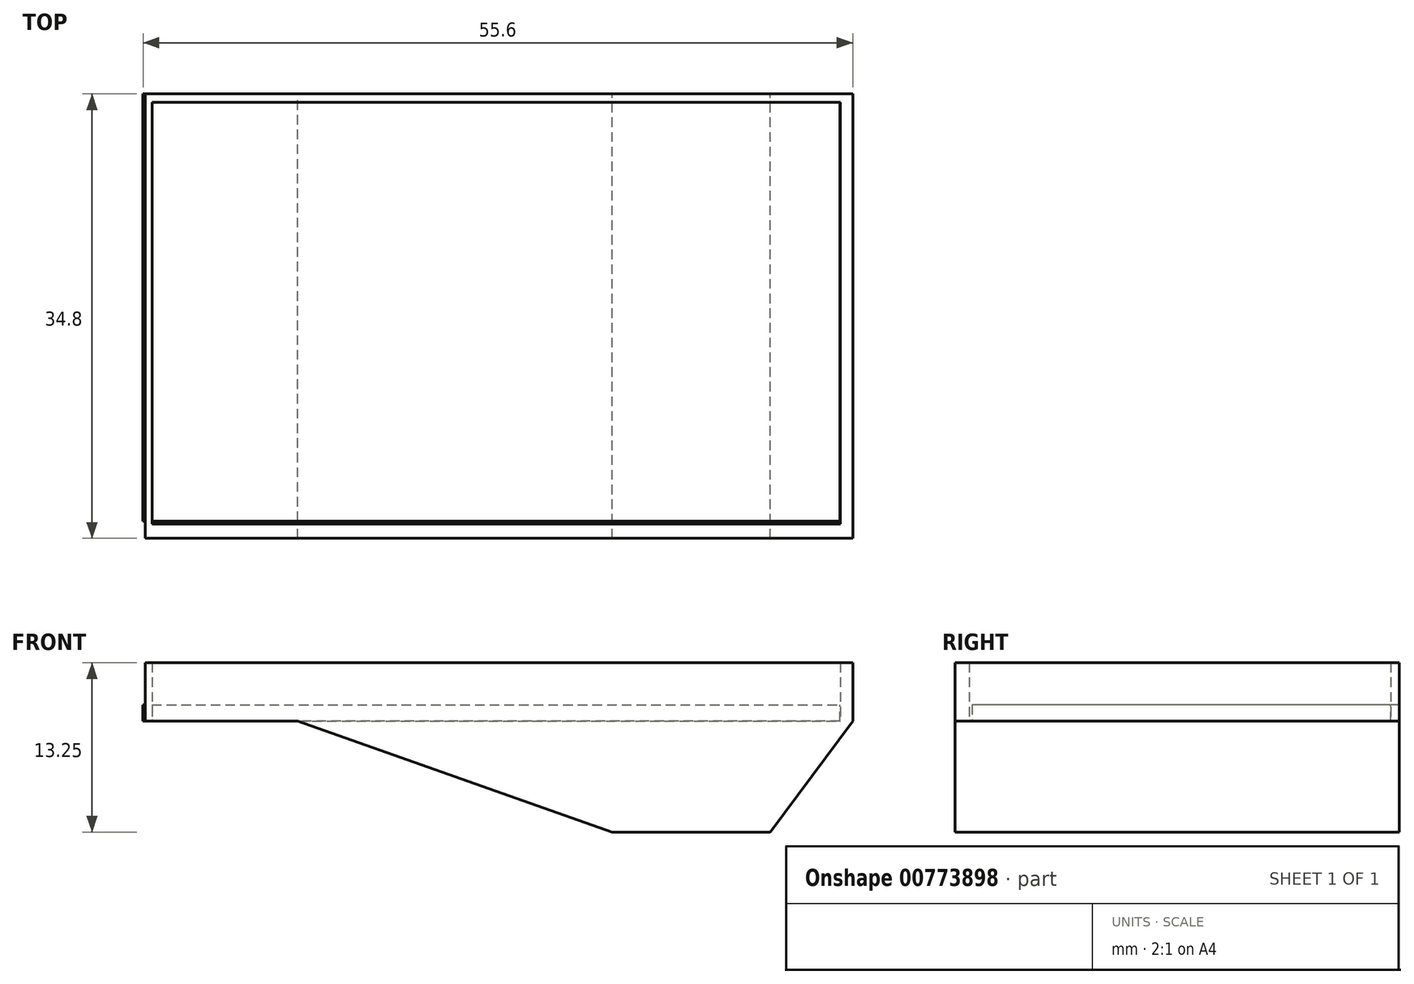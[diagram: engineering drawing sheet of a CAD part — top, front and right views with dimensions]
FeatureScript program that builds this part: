
annotation { "Feature Type Name" : "Feature", "Feature Type Description" : "" }
export const myFeature = defineFeature(function(context is Context, id is Id, definition is map)
    precondition{}
    {
        {
            var Q0;
            Q0=qCreatedBy(makeId("Top.planeOp"),FACE);
            var sketch = newSketch(context, id + "F0", { "sketchPlane" : qUnion([Q0])});
            skLineSegment(sketch, "E0.bottom", {"start": v(5.13, 0) * mm, "end": v(60.56, 0) * mm});
            skLineSegment(sketch, "E0.top", {"start": v(5.13, -34.8) * mm, "end": v(60.56, -34.8) * mm});
            skLineSegment(sketch, "E0.left", {"start": v(5.13, 0) * mm, "end": v(5.13, -34.8) * mm});
            skLineSegment(sketch, "E0.right", {"start": v(60.56, 0) * mm, "end": v(60.56, -34.8) * mm});
            skLineSegment(sketch, "E1.bottom", {"start": v(5.66, -0.66) * mm, "end": v(59.57, -0.66) * mm});
            skLineSegment(sketch, "E1.top", {"start": v(5.66, -33.68) * mm, "end": v(59.57, -33.68) * mm});
            skLineSegment(sketch, "E1.left", {"start": v(5.66, -0.66) * mm, "end": v(5.66, -33.68) * mm});
            skLineSegment(sketch, "E1.right", {"start": v(59.57, -0.66) * mm, "end": v(59.57, -33.68) * mm});
            skSolve(sketch);
        }
        {
            var Q0;
            Q0 = qSketchRegion(id + "F0", true);
            extrude(context, id + "F1", {"entities" : qUnion([Q0]), "depth" : 4.57 * mm, "offsetDistance" : 25.4 * mm});
        }
        {
            var Q0;
            Q0=qCreatedBy(makeId("Top.planeOp"),FACE);
            var sketch = newSketch(context, id + "F2", { "sketchPlane" : qUnion([Q0])});
            skLineSegment(sketch, "E2.bottom", {"start": v(59.56, -33.46) * mm, "end": v(4.96, -33.46) * mm});
            skLineSegment(sketch, "E2.top", {"start": v(59.56, 0) * mm, "end": v(4.96, 0) * mm});
            skLineSegment(sketch, "E2.left", {"start": v(59.56, -33.46) * mm, "end": v(59.56, 0) * mm});
            skLineSegment(sketch, "E2.right", {"start": v(4.96, -33.46) * mm, "end": v(4.96, 0) * mm});
            skSolve(sketch);
        }
        {
            var Q0;
            Q0=makeQuery(id+"F2.imprint","IMPRINT",FACE,{"disambiguationData":[TD([[makeQuery(id+"F2.imprint","IMPRINT",EDGE,{"derivedFrom":sQuery(id+"F2.wireOp",EDGE,"E2.bottom")}),-1.0]])]});
            extrude(context, id + "F3", {"entities" : qUnion([Q0]), "operationType" : NewBodyOperationType.ADD, "depth" : 1.27 * mm, "offsetDistance" : 25.4 * mm});
        }
        {
            var Q0;
            Q0=makeQuery(id+"F3.boolean.opBoolean","MERGE",FACE,{"derivedFrom":[makeQuery(id+"F1.opExtrude","SWEPT_FACE",FACE,{"disambiguationData":[OSD([sQuery(id+"F0.wireOp",EDGE,"E0.bottom")])]}),makeQuery(id+"F3.opExtrude","SWEPT_FACE",FACE,{"disambiguationData":[OSD([sQuery(id+"F2.wireOp",EDGE,"E2.top")])]})]});
            var sketch = newSketch(context, id + "F4", { "sketchPlane" : qUnion([Q0])});
            skLineSegment(sketch, "E3.bottom", {"start": v(-54.09, 0) * mm, "end": v(-41.71, 0) * mm});
            skLineSegment(sketch, "E3.top", {"start": v(-54.09, -8.68) * mm, "end": v(-41.71, -8.68) * mm});
            skLineSegment(sketch, "E4", {"start": v(-60.56, 0) * mm, "end": v(-54.09, -8.68) * mm});
            skLineSegment(sketch, "E5", {"start": v(-41.71, -8.68) * mm, "end": v(-17.07, 0) * mm});
            skLineSegment(sketch, "E6", {"start": v(-17.07, 0) * mm, "end": v(-60.56, 0) * mm});
            skSolve(sketch);
        }
        {
            var Q0;
            Q0 = qSketchRegion(id + "F4", true);
            var Q1;
            Q1=makeQuery(id+"F1.opExtrude","SWEPT_FACE",FACE,{"disambiguationData":[OSD([sQuery(id+"F0.wireOp",EDGE,"E0.top")])]});
            extrude(context, id + "F5", {"entities" : qUnion([Q0]), "operationType" : NewBodyOperationType.ADD, "endBound" : BoundingType.UP_TO_SURFACE, "oppositeDirection" : true, "depth" : 25.4 * mm, "endBoundEntityFace" : qUnion([Q1]), "offsetDistance" : 25.4 * mm});
        }
        {
            var Q0;
            {var subQ0=sQuery(id+"F2.wireOp",EDGE,"E2.left");var subQ1=sQuery(id+"F2.wireOp",EDGE,"E2.bottom");Q0=makeQuery(id+"F3.boolean.opBoolean","SPLIT",FACE,{"disambiguationData":[TD([makeQuery(id+"F1.opExtrude","SWEPT_FACE",FACE,{"disambiguationData":[OSD([sQuery(id+"F0.wireOp",EDGE,"E1.bottom")])]})])],"derivedFrom":makeQuery(id+"F3.opExtrude","CAP_FACE",FACE,{"disambiguationData":[OSD([subQ1,sQuery(id+"F2.wireOp",EDGE,"E2.top"),subQ0,sQuery(id+"F2.wireOp",EDGE,"E2.right")])],"isStart":false})});}
            var sketch = newSketch(context, id + "F6", { "sketchPlane" : qUnion([Q0])});
            skLineSegment(sketch, "E7.bottom", {"start": v(59.56, -33.46) * mm, "end": v(53.74, -33.46) * mm});
            skLineSegment(sketch, "E7.top", {"start": v(59.56, -0.66) * mm, "end": v(53.74, -0.66) * mm});
            skLineSegment(sketch, "E7.left", {"start": v(59.56, -33.46) * mm, "end": v(59.56, -0.66) * mm});
            skLineSegment(sketch, "E7.right", {"start": v(53.74, -33.46) * mm, "end": v(53.74, -0.66) * mm});
            skLineSegment(sketch, "E8", {"start": v(58.14, -0.66) * mm, "end": v(58.14, -33.46) * mm});
            skLineSegment(sketch, "E9", {"start": v(58.14, -33.46) * mm, "end": v(56.65, -33.46) * mm});
            skLineSegment(sketch, "E10", {"start": v(56.65, -33.46) * mm, "end": v(56.65, -0.66) * mm});
            skLineSegment(sketch, "E11", {"start": v(56.65, -0.66) * mm, "end": v(54.7, -0.66) * mm});
            skLineSegment(sketch, "E12", {"start": v(54.7, -0.66) * mm, "end": v(54.7, -33.46) * mm});
            skLineSegment(sketch, "E13.bottom", {"start": v(53.74, -33.46) * mm, "end": v(39.9, -33.46) * mm});
            skLineSegment(sketch, "E13.top", {"start": v(53.74, -0.66) * mm, "end": v(39.9, -0.66) * mm});
            skLineSegment(sketch, "E13.right", {"start": v(39.9, -33.46) * mm, "end": v(39.9, -0.66) * mm});
            skSolve(sketch);
        }
        {
            var Q0;
            Q0=makeQuery(id+"F6.imprint","IMPRINT",FACE,{"disambiguationData":[TD([[makeQuery(id+"F6.imprint","IMPRINT",EDGE,{"derivedFrom":sQuery(id+"F6.wireOp",EDGE,"E13.bottom")}),-1.0]])]});
            extrude(context, id + "F7", {"entities" : qUnion([Q0]), "operationType" : NewBodyOperationType.ADD, "oppositeDirection" : true, "depth" : 8.38 * mm, "offsetDistance" : 25.4 * mm});
        }
    });
